# Revit family: QF_FESTIVE_YA12
name_source: partatom
category: Specialty Equipment
units: mm (PartAtom-declared; Revit-internal decimal feet)

## family parameters
Always vertical = Yes
Cut with Voids When Loaded = No
Part Type = Normal
Room Calculation Point = No
Round Connector Dimension = Use Diameter
Shared = No
Work Plane-Based = No

## types (1)
- YA12_220-240/50/1
    Apparent Power = 132 VA
    Conn Conduit = Yes
    Conn Plug = 10A Plug
    Cycle = 50 Hz
    Default Elevation = 0 mm  [stored 0 ft]
    Depth = 640 mm  [stored 2.09974 ft]
    Description = YORK AMBIENT
    Elec Conn Connection Height = 0 mm  [stored 0 ft]
    Elec Conn RI Height = 0 mm  [stored 0 ft]
    FL Amps = 1 A
    Foodservice Equipment Identifier = Yes
    Height = 1400 mm  [stored 4.59318 ft]
    Identify Quantity as Lot = Yes
    Length = 1200 mm
    Manufacturer = FESTIVE
    Max Overcurrent Protection = 0 A
    Min Ckt Ampacity = 0 A
    Model = YA12
    Number of Poles = 1
    Phase = 1
    Volts = 220 V
    Watts = 132 W
    Weight in Pounds = 0

note: [stored X ft] marks values corroborated as IEEE doubles in the binary element streams (Revit-internal decimal feet)

## geometry (parser evidence)
native form markers: Sweep x10
no freeform markers — native parametric forms only
